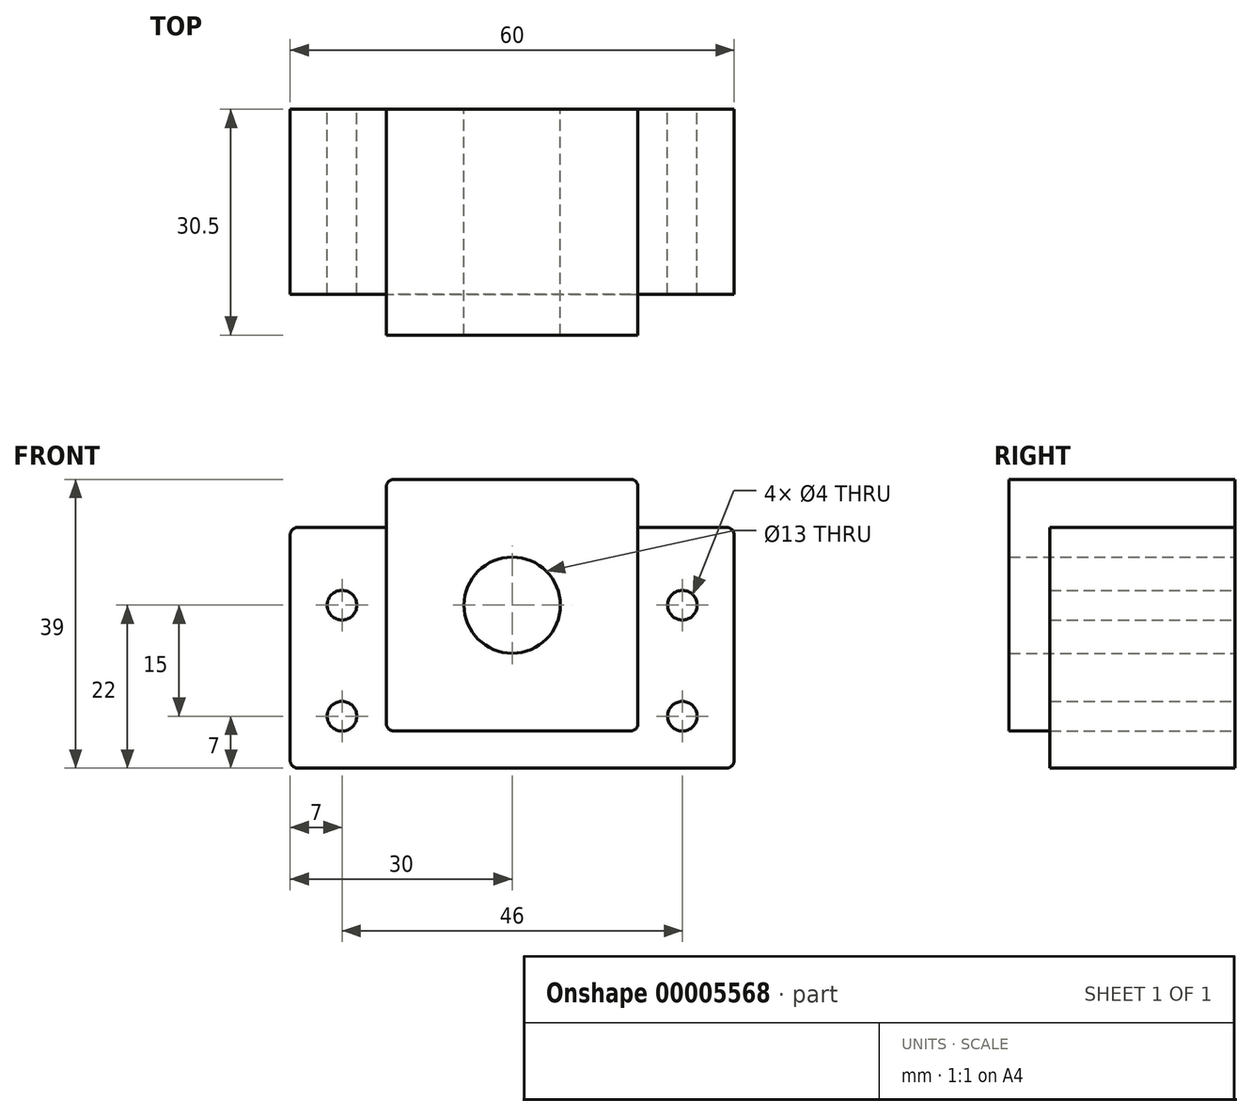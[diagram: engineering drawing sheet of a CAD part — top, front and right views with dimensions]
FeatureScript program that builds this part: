
annotation { "Feature Type Name" : "Feature", "Feature Type Description" : "" }
export const myFeature = defineFeature(function(context is Context, id is Id, definition is map)
    precondition{}
    {
        {
            var Q0;
            Q0=qCreatedBy(makeId("Front.planeOp"),FACE);
            var sketch = newSketch(context, id + "F0", { "sketchPlane" : qUnion([Q0])});
            skLineSegment(sketch, "E0.bottom", {"start": v(-29, 10.5) * mm, "end": v(29, 10.5) * mm});
            skLineSegment(sketch, "E0.top", {"start": v(-29, -22) * mm, "end": v(29, -22) * mm});
            skLineSegment(sketch, "E0.left", {"start": v(-30, 9.5) * mm, "end": v(-30, -21) * mm});
            skLineSegment(sketch, "E0.right", {"start": v(30, 9.5) * mm, "end": v(30, -21) * mm});
            skCircle(sketch, "E1", {"center": v(0, 0) * mm, "radius": 6.5 * mm});
            skLineSegment(sketch, "E2", {"start": v(0, 10.5) * mm, "end": v(0, -22) * mm, "construction": true});
            skLineSegment(sketch, "E3", {"start": v(-30, 0) * mm, "end": v(30, 0) * mm, "construction": true});
            skCircle(sketch, "E4", {"center": v(-23, 0) * mm, "radius": 2 * mm});
            skCircle(sketch, "E5.0.MirrorC", {"center": v(23, 0) * mm, "radius": 2 * mm});
            skLineSegment(sketch, "E6", {"start": v(-30, -7.5) * mm, "end": v(30, -7.5) * mm, "construction": true});
            skCircle(sketch, "E7.0.MirrorC", {"center": v(-23, -15) * mm, "radius": 2 * mm});
            skCircle(sketch, "E8.0.MirrorC", {"center": v(23, -15) * mm, "radius": 2 * mm});
            skPoint(sketch, "E9.visualSharp", {"position": v(-30, 10.5) * mm});
            skArc(sketch, "E9.filletArc", {"start": v(-29, 10.5) * mm, "mid": v(-29.7, 10.2) * mm, "end": v(-30, 9.5) * mm});
            skPoint(sketch, "E10.visualSharp", {"position": v(30, 10.5) * mm});
            skArc(sketch, "E10.filletArc", {"start": v(30, 9.5) * mm, "mid": v(29.7, 10.2) * mm, "end": v(29, 10.5) * mm});
            skPoint(sketch, "E11.visualSharp", {"position": v(30, -22) * mm});
            skArc(sketch, "E11.filletArc", {"start": v(29, -22) * mm, "mid": v(29.7, -21.7) * mm, "end": v(30, -21) * mm});
            skPoint(sketch, "E12.visualSharp", {"position": v(-30, -22) * mm});
            skArc(sketch, "E12.filletArc", {"start": v(-30, -21) * mm, "mid": v(-29.7, -21.7) * mm, "end": v(-29, -22) * mm});
            skSolve(sketch);
        }
        {
            var Q0;
            Q0=makeQuery(id+"F0.imprint","IMPRINT",FACE,{"disambiguationData":[TD([[makeQuery(id+"F0.imprint","IMPRINT",EDGE,{"derivedFrom":sQuery(id+"F0.wireOp",EDGE,"E0.bottom")}),-1.0]])]});
            extrude(context, id + "F1", {"entities" : qUnion([Q0]), "depth" : 25 * mm});
        }
        {
            var Q0;
            Q0=qCreatedBy(makeId("Front.planeOp"),FACE);
            var sketch = newSketch(context, id + "F2", { "sketchPlane" : qUnion([Q0])});
            skLineSegment(sketch, "E13.bottom", {"start": v(-16, 17) * mm, "end": v(16, 17) * mm});
            skLineSegment(sketch, "E13.top", {"start": v(-16, -17) * mm, "end": v(16, -17) * mm});
            skLineSegment(sketch, "E13.left", {"start": v(-17, 16) * mm, "end": v(-17, -16) * mm});
            skLineSegment(sketch, "E13.right", {"start": v(17, 16) * mm, "end": v(17, -16) * mm});
            skLineSegment(sketch, "E14", {"start": v(0, 17) * mm, "end": v(0, -17) * mm, "construction": true});
            skLineSegment(sketch, "E15", {"start": v(-17, 0) * mm, "end": v(17, 0) * mm, "construction": true});
            skPoint(sketch, "E16.visualSharp", {"position": v(-17, 17) * mm});
            skArc(sketch, "E16.filletArc", {"start": v(-16, 17) * mm, "mid": v(-16.7, 16.7) * mm, "end": v(-17, 16) * mm});
            skPoint(sketch, "E17.visualSharp", {"position": v(17, 17) * mm});
            skArc(sketch, "E17.filletArc", {"start": v(17, 16) * mm, "mid": v(16.7, 16.7) * mm, "end": v(16, 17) * mm});
            skPoint(sketch, "E18.visualSharp", {"position": v(17, -17) * mm});
            skArc(sketch, "E18.filletArc", {"start": v(16, -17) * mm, "mid": v(16.7, -16.7) * mm, "end": v(17, -16) * mm});
            skPoint(sketch, "E19.visualSharp", {"position": v(-17, -17) * mm});
            skArc(sketch, "E19.filletArc", {"start": v(-17, -16) * mm, "mid": v(-16.7, -16.7) * mm, "end": v(-16, -17) * mm});
            skCircle(sketch, "E20", {"center": v(0, 0) * mm, "radius": 6.5 * mm});
            skSolve(sketch);
        }
        {
            var Q0;
            Q0=makeQuery(id+"F2.imprint","IMPRINT",FACE,{"disambiguationData":[TD([[makeQuery(id+"F2.imprint","IMPRINT",EDGE,{"derivedFrom":sQuery(id+"F2.wireOp",EDGE,"E13.bottom")}),-1.0]])]});
            extrude(context, id + "F3", {"entities" : qUnion([Q0]), "operationType" : NewBodyOperationType.ADD, "depth" : 30.5 * mm});
        }
    });
